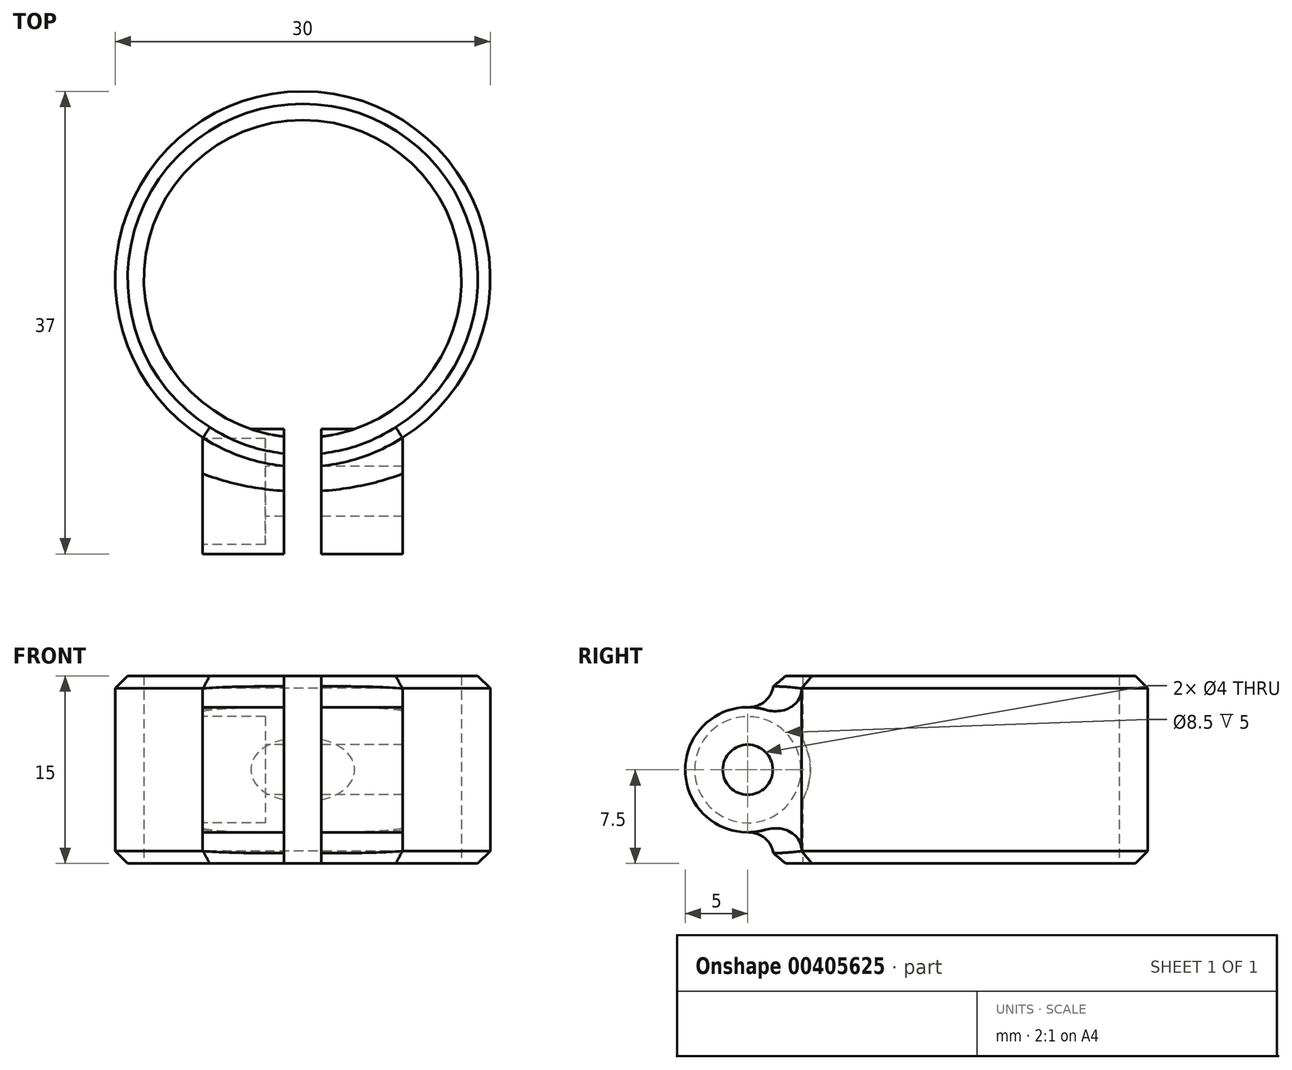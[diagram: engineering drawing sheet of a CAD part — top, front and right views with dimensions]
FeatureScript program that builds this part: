
annotation { "Feature Type Name" : "Feature", "Feature Type Description" : "" }
export const myFeature = defineFeature(function(context is Context, id is Id, definition is map)
    precondition{}
    {
        {
            var Q0;
            Q0=qCreatedBy(makeId("Top.planeOp"),FACE);
            var sketch = newSketch(context, id + "F0", { "sketchPlane" : qUnion([Q0])});
            skCircle(sketch, "E0", {"center": v(0, 0) * mm, "radius": 12.7 * mm});
            skCircle(sketch, "E1", {"center": v(0, 0) * mm, "radius": 15 * mm});
            skSolve(sketch);
        }
        {
            var Q0;
            Q0=makeQuery(id+"F0.imprint","IMPRINT",FACE,{"disambiguationData":[TD([[makeQuery(id+"F0.imprint","IMPRINT",EDGE,{"derivedFrom":sQuery(id+"F0.wireOp",EDGE,"E0")}),-1.0]])]});
            extrude(context, id + "F1", {"entities" : qUnion([Q0]), "depth" : 7.5 * mm, "hasSecondDirection" : true, "secondDirectionOppositeDirection" : true, "secondDirectionDepth" : 7.5 * mm});
        }
        {
            var Q0;
            Q0=qCreatedBy(makeId("Right.planeOp"),FACE);
            var sketch = newSketch(context, id + "F2", { "sketchPlane" : qUnion([Q0])});
            skLineSegment(sketch, "E2", {"start": v(0, 0) * mm, "end": v(-26.6, 0) * mm, "construction": true});
            skLineSegment(sketch, "E3", {"start": v(0, 0) * mm, "end": v(0, 19) * mm, "construction": true});
            skCircle(sketch, "E4", {"center": v(-17, 0) * mm, "radius": 5 * mm});
            skSolve(sketch);
        }
        {
            var Q0;
            Q0 = qSketchRegion(id + "F2", true);
            extrude(context, id + "F3", {"entities" : qUnion([Q0]), "operationType" : NewBodyOperationType.ADD, "depth" : 8 * mm, "hasSecondDirection" : true, "secondDirectionOppositeDirection" : true, "secondDirectionDepth" : 8 * mm});
        }
        {
            var Q0;
            Q0=qCreatedBy(makeId("Top.planeOp"),FACE);
            var sketch = newSketch(context, id + "F4", { "sketchPlane" : qUnion([Q0])});
            skLineSegment(sketch, "E5.bottom", {"start": v(1.5, -10) * mm, "end": v(-1.5, -10) * mm});
            skLineSegment(sketch, "E5.top", {"start": v(1.5, -25) * mm, "end": v(-1.5, -25) * mm});
            skLineSegment(sketch, "E5.left", {"start": v(1.5, -10) * mm, "end": v(1.5, -25) * mm});
            skLineSegment(sketch, "E5.right", {"start": v(-1.5, -10) * mm, "end": v(-1.5, -25) * mm});
            skPoint(sketch, "E5.middle", {"position": v(0, -17.5) * mm});
            skSolve(sketch);
        }
        {
            var Q0;
            Q0=makeQuery(id+"F4.imprint","IMPRINT",FACE,{"disambiguationData":[TD([[makeQuery(id+"F4.imprint","IMPRINT",EDGE,{"derivedFrom":sQuery(id+"F4.wireOp",EDGE,"E5.bottom")}),1.0]])]});
            extrude(context, id + "F5", {"entities" : qUnion([Q0]), "operationType" : NewBodyOperationType.REMOVE, "endBound" : BoundingType.THROUGH_ALL, "oppositeDirection" : true, "depth" : 25 * mm, "hasSecondDirection" : true, "secondDirectionOppositeDirection" : false, "secondDirectionDepth" : 25 * mm});
        }
        {
            var Q0;
            {var subQ0=makeQuery(id+"F1.opExtrude","SWEPT_FACE",FACE,{"disambiguationData":[OSD([sQuery(id+"F0.wireOp",EDGE,"E1")])]});var subQ1=makeQuery(id+"F3.opExtrude","SWEPT_FACE",FACE,{"disambiguationData":[OSD([sQuery(id+"F2.wireOp",EDGE,"E4")])]});Q0=makeQuery(id+"F5.boolean.opBoolean","SPLIT",EDGE,{"disambiguationData":[TD([makeQuery(id+"F5.opExtrude","SWEPT_FACE",FACE,{"disambiguationData":[OSD([sQuery(id+"F4.wireOp",EDGE,"E5.left")])]})])],"derivedFrom":makeQuery(id+"F3.boolean.opBoolean","INTERSECT",EDGE,{"derivedFrom":[subQ0,subQ1]})});}
            var Q1;
            {var subQ0=makeQuery(id+"F1.opExtrude","SWEPT_FACE",FACE,{"disambiguationData":[OSD([sQuery(id+"F0.wireOp",EDGE,"E1")])]});var subQ1=makeQuery(id+"F3.opExtrude","SWEPT_FACE",FACE,{"disambiguationData":[OSD([sQuery(id+"F2.wireOp",EDGE,"E4")])]});Q1=makeQuery(id+"F5.boolean.opBoolean","SPLIT",EDGE,{"disambiguationData":[TD([makeQuery(id+"F5.opExtrude","SWEPT_FACE",FACE,{"disambiguationData":[OSD([sQuery(id+"F4.wireOp",EDGE,"E5.right")])]})])],"derivedFrom":makeQuery(id+"F3.boolean.opBoolean","INTERSECT",EDGE,{"derivedFrom":[subQ0,subQ1]})});}
            fillet(context, id + "F6", {"entities" : qUnion([Q0, Q1]), "radius" : 2 * mm, "tangentPropagation" : true, "allowEdgeOverflow" : false});
        }
        {
            var Q0;
            Q0=makeQuery(id+"F1.opExtrude","CAP_EDGE",EDGE,{"disambiguationData":[OSD([sQuery(id+"F0.wireOp",EDGE,"E1")])],"isStart":false});
            var Q1;
            Q1=makeQuery(id+"F1.opExtrude","CAP_EDGE",EDGE,{"disambiguationData":[OSD([sQuery(id+"F0.wireOp",EDGE,"E1")])],"isStart":true});
            chamfer(context, id + "F7", {"entities" : qUnion([Q0, Q1]), "width" : 1 * mm, "tangentPropagation" : true});
        }
        {
            var Q0;
            Q0=makeQuery(id+"F3.opExtrude","CAP_FACE",FACE,{"disambiguationData":[OSD([sQuery(id+"F2.wireOp",EDGE,"E4")])],"isStart":true});
            var sketch = newSketch(context, id + "F8", { "sketchPlane" : qUnion([Q0])});
            skCircle(sketch, "E6", {"center": v(17, 0) * mm, "radius": 4.25 * mm});
            skSolve(sketch);
        }
        {
            var Q0;
            Q0=makeQuery(id+"F8.imprint","IMPRINT",FACE,{"disambiguationData":[TD([[makeQuery(id+"F8.imprint","IMPRINT",EDGE,{"derivedFrom":sQuery(id+"F8.wireOp",EDGE,"E6")}),1.0]])]});
            extrude(context, id + "F9", {"entities" : qUnion([Q0]), "operationType" : NewBodyOperationType.REMOVE, "oppositeDirection" : true, "depth" : 5 * mm});
        }
        {
            var Q0;
            Q0=makeQuery(id+"F9.boolean.opBoolean","COPY",FACE,{"derivedFrom":makeQuery(id+"F9.opExtrude","CAP_FACE",FACE,{"disambiguationData":[OSD([sQuery(id+"F8.wireOp",EDGE,"E6")])],"isStart":false})});
            var sketch = newSketch(context, id + "F10", { "sketchPlane" : qUnion([Q0])});
            skCircle(sketch, "E7", {"center": v(17, 0) * mm, "radius": 2 * mm});
            skSolve(sketch);
        }
        {
            var Q0;
            Q0=makeQuery(id+"F10.imprint","IMPRINT",FACE,{"disambiguationData":[TD([[makeQuery(id+"F10.imprint","IMPRINT",EDGE,{"derivedFrom":sQuery(id+"F10.wireOp",EDGE,"E7")}),1.0]])]});
            extrude(context, id + "F11", {"entities" : qUnion([Q0]), "operationType" : NewBodyOperationType.REMOVE, "endBound" : BoundingType.THROUGH_ALL, "oppositeDirection" : true, "depth" : 25 * mm});
        }
    });
